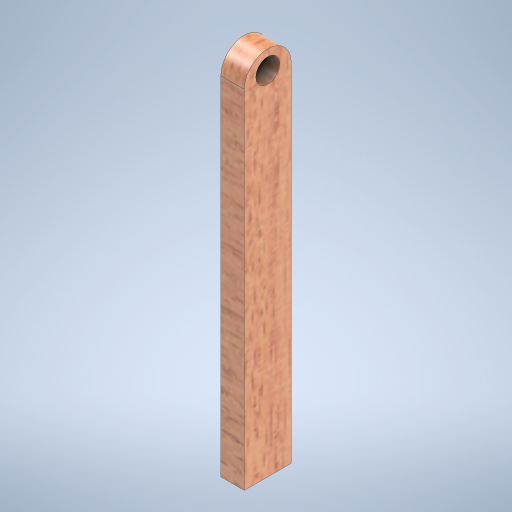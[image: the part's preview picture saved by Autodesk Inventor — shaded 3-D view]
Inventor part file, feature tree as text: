
AUTODESK INVENTOR PART (.ipt)
format: ipt  version: 2023 (Build 270158000, 158)  size: 329,728 bytes
history: native  units: mm
features: sketch x2, extrude x1, hole x1, fillet x1
ambient origin geometry x8: Origin, YZ Plane, XZ Plane, XY Plane, X Axis, Y Axis, Z Axis, Center Point
bodies: Volumenkörper1 (feature_tree)
feature tree (5):
  extrude  "Extrusion1"  Depth=20.0mm
  hole  "Bohrung1"  [1 undecoded]
  fillet  "Rundung1"  Radius=10.0mm
  sketch  "Skizze1"  dims[d0=158.0mm d1=20.0mm]
  sketch  "Skizze2"  dims[d2=10.0mm d3=0.0mm d4=10.2mm d5=6.0mm d6=4.0mm d7=2.0mm d8=90.0deg d9=8.0mm d10=20.594885mm d11=150.0mm d12=10.0mm d13=10.0mm]
note: 1 required parameter value undecoded (feature->parameter linkage not recoverable at this tier; creation-order binding heuristic only, values carry confidence <= 0.55)
